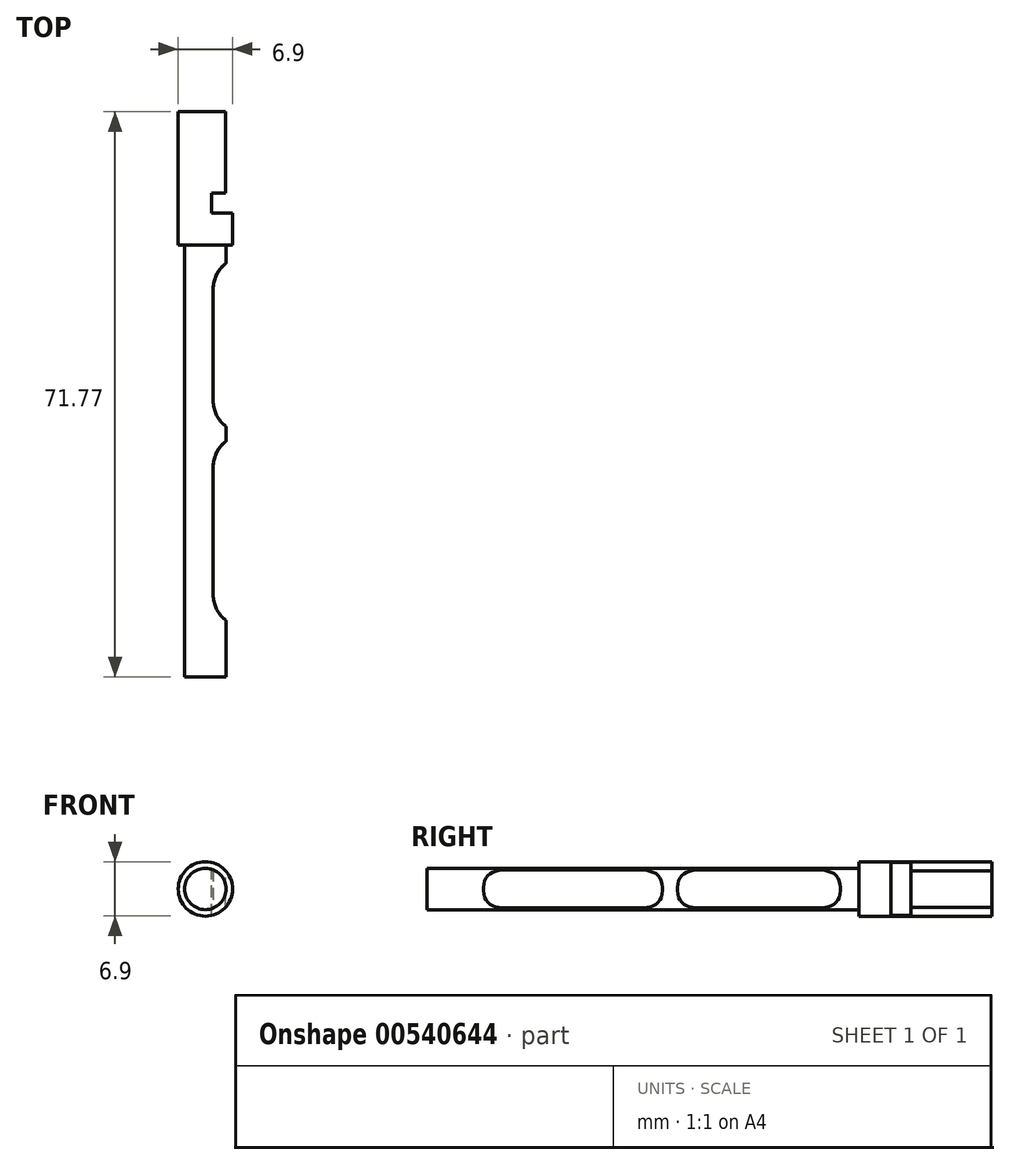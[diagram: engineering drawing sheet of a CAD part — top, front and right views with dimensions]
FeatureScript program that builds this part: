
annotation { "Feature Type Name" : "Feature", "Feature Type Description" : "" }
export const myFeature = defineFeature(function(context is Context, id is Id, definition is map)
    precondition{}
    {
        {
            var Q0;
            Q0=qCreatedBy(makeId("Front.planeOp"),FACE);
            var sketch = newSketch(context, id + "F0", { "sketchPlane" : qUnion([Q0])});
            skCircle(sketch, "E0", {"center": v(0, 0) * mm, "radius": 3.45 * mm});
            skSolve(sketch);
        }
        {
            var Q0;
            Q0 = qSketchRegion(id + "F0", true);
            extrude(context, id + "F1", {"entities" : qUnion([Q0]), "depth" : 71.77 * mm, "offsetDistance" : 25.4 * mm});
        }
        {
            var Q0;
            Q0=qCreatedBy(makeId("Top.planeOp"),FACE);
            cPlane(context, id + "F2", {"entities" : qUnion([Q0]), "cplaneType" : CPlaneType.OFFSET, "offset" : 25.4 * mm, "width" : 152.4 * mm, "height" : 152.4 * mm});
        }
        {
            var Q0;
            Q0=qCreatedBy(id+"F2.planeOp",FACE);
            var sketch = newSketch(context, id + "F3", { "sketchPlane" : qUnion([Q0])});
            skLineSegment(sketch, "E1", {"start": v(0.76, -12.84) * mm, "end": v(5.6, -12.84) * mm});
            skLineSegment(sketch, "E2", {"start": v(0.76, -10.33) * mm, "end": v(5.6, -10.33) * mm});
            skLineSegment(sketch, "E3", {"start": v(0.76, -12.84) * mm, "end": v(0.76, -10.33) * mm});
            skLineSegment(sketch, "E4", {"start": v(5.6, -12.84) * mm, "end": v(5.6, -10.33) * mm});
            skPoint(sketch, "E5.orphan", {"position": v(0.76, 0) * mm});
            skSolve(sketch);
        }
        {
            var Q0;
            Q0=makeQuery(id+"F3.imprint","IMPRINT",FACE,{"disambiguationData":[TD([[makeQuery(id+"F3.imprint","IMPRINT",EDGE,{"derivedFrom":sQuery(id+"F3.wireOp",EDGE,"E1")}),1.0]])]});
            extrude(context, id + "F4", {"entities" : qUnion([Q0]), "operationType" : NewBodyOperationType.REMOVE, "oppositeDirection" : true, "depth" : 39.88 * mm, "offsetDistance" : 25.4 * mm});
        }
        {
            var Q0;
            Q0=qCreatedBy(id+"F2.planeOp",FACE);
            var sketch = newSketch(context, id + "F5", { "sketchPlane" : qUnion([Q0])});
            skLineSegment(sketch, "E6", {"start": v(0, 0) * mm, "end": v(0, -14.35) * mm});
            skLineSegment(sketch, "E7", {"start": v(2.57, 0) * mm, "end": v(2.57, -11.2) * mm});
            skLineSegment(sketch, "E8", {"start": v(2.57, -11.2) * mm, "end": v(5.53, -11.2) * mm});
            skLineSegment(sketch, "E9", {"start": v(5.53, 0) * mm, "end": v(5.53, -11.2) * mm});
            skLineSegment(sketch, "E10", {"start": v(2.57, 0) * mm, "end": v(5.53, 0) * mm});
            skSolve(sketch);
        }
        {
            var Q0;
            Q0 = qSketchRegion(id + "F5", true);
            extrude(context, id + "F6", {"entities" : qUnion([Q0]), "operationType" : NewBodyOperationType.REMOVE, "oppositeDirection" : true, "depth" : 56.64 * mm, "offsetDistance" : 25.4 * mm});
        }
        {
            var Q0;
            Q0=makeQuery(id+"F4.boolean.opBoolean","COPY",FACE,{"derivedFrom":makeQuery(id+"F4.opExtrude","SWEPT_FACE",FACE,{"disambiguationData":[OSD([sQuery(id+"F3.wireOp",EDGE,"E1")])]})});
            cPlane(context, id + "F7", {"entities" : qUnion([Q0]), "cplaneType" : CPlaneType.OFFSET, "offset" : 4.06 * mm, "oppositeDirection" : true, "width" : 152.4 * mm, "height" : 152.4 * mm});
        }
        {
            var Q0;
            Q0=qCreatedBy(id+"F7.planeOp",FACE);
            var sketch = newSketch(context, id + "F8", { "sketchPlane" : qUnion([Q0])});
            skCircle(sketch, "E11", {"center": v(0, 0) * mm, "radius": 2.63 * mm});
            skCircle(sketch, "E12", {"center": v(0, 0) * mm, "radius": 3.45 * mm});
            skSolve(sketch);
        }
        {
            var Q0;
            Q0 = qSketchRegion(id + "F8", true);
            extrude(context, id + "F9", {"entities" : qUnion([Q0]), "operationType" : NewBodyOperationType.REMOVE, "oppositeDirection" : true, "depth" : 58.42 * mm, "offsetDistance" : 25.4 * mm});
        }
        {
            var Q0;
            Q0=qCreatedBy(makeId("Top.planeOp"),FACE);
            var sketch = newSketch(context, id + "F10", { "sketchPlane" : qUnion([Q0])});
            skLineSegment(sketch, "E13.0", {"start": v(1, -45.1) * mm, "end": v(1, -61.36) * mm});
            skArc(sketch, "E14", {"start": v(5.05, -18.43) * mm, "mid": v(2.18, -19.62) * mm, "end": v(1, -22.5) * mm});
            skLineSegment(sketch, "E15", {"start": v(1, -22.5) * mm, "end": v(1, -36.72) * mm});
            skArc(sketch, "E16", {"start": v(1, -36.72) * mm, "mid": v(2.18, -39.6) * mm, "end": v(5.05, -40.78) * mm});
            skArc(sketch, "E17", {"start": v(5.05, -41.04) * mm, "mid": v(2.18, -42.23) * mm, "end": v(1, -45.1) * mm});
            skArc(sketch, "E18", {"start": v(1, -61.36) * mm, "mid": v(2.18, -64.23) * mm, "end": v(5.05, -65.42) * mm});
            skLineSegment(sketch, "E19", {"start": v(5.05, -18.43) * mm, "end": v(5.05, -40.78) * mm});
            skLineSegment(sketch, "E20", {"start": v(5.05, -41.04) * mm, "end": v(5.05, -65.42) * mm});
            skSolve(sketch);
        }
        {
            var Q0;
            Q0 = qSketchRegion(id + "F10", true);
            extrude(context, id + "F11", {"entities" : qUnion([Q0]), "operationType" : NewBodyOperationType.REMOVE, "depth" : 25.4 * mm, "offsetDistance" : 25.4 * mm});
        }
        {
            var Q0;
            Q0=makeQuery(id+"F11.boolean.opBoolean","COPY",FACE,{"derivedFrom":makeQuery(id+"F11.opExtrude","CAP_FACE",FACE,{"disambiguationData":[OSD([sQuery(id+"F10.wireOp",EDGE,"E17"),sQuery(id+"F10.wireOp",EDGE,"E18"),sQuery(id+"F10.wireOp",EDGE,"E20"),sQuery(id+"F10.wireOp",EDGE,"E13.0")])],"isStart":true})});
            var sketch = newSketch(context, id + "F12", { "sketchPlane" : qUnion([Q0])});
            skSolve(sketch);
        }
        {
            var Q0;
            Q0 = qSketchRegion(id + "F12", true);
            var Q1;
            {var subQ0=sQuery(id+"F10.wireOp",EDGE,"E17");Q1=makeQuery(id+"F12.imprint","IMPRINT",FACE,{"disambiguationData":[TD([[makeQuery(id+"F12.imprint","IMPRINT",EDGE,{"derivedFrom":makeQuery(id+"F11.boolean.opBoolean","COPY",EDGE,{"derivedFrom":makeQuery(id+"F11.opExtrude","CAP_EDGE",EDGE,{"disambiguationData":[OSD([subQ0])],"isStart":true})})}),1.0]])]});}
            extrude(context, id + "F13", {"entities" : qUnion([Q0, Q1]), "operationType" : NewBodyOperationType.REMOVE, "oppositeDirection" : true, "depth" : 25.4 * mm, "offsetDistance" : 25.4 * mm});
        }
        {
            var Q0;
            Q0=makeQuery(id+"F11.boolean.opBoolean","COPY",FACE,{"derivedFrom":makeQuery(id+"F11.opExtrude","CAP_FACE",FACE,{"disambiguationData":[OSD([sQuery(id+"F10.wireOp",EDGE,"E14"),sQuery(id+"F10.wireOp",EDGE,"E16"),sQuery(id+"F10.wireOp",EDGE,"E15"),sQuery(id+"F10.wireOp",EDGE,"E19")])],"isStart":true})});
            var sketch = newSketch(context, id + "F14", { "sketchPlane" : qUnion([Q0])});
            skSolve(sketch);
        }
        {
            var Q0;
            Q0 = qSketchRegion(id + "F14", true);
            var Q1;
            {var subQ0=sQuery(id+"F10.wireOp",EDGE,"E14");Q1=makeQuery(id+"F14.imprint","IMPRINT",FACE,{"disambiguationData":[TD([[makeQuery(id+"F14.imprint","IMPRINT",EDGE,{"derivedFrom":makeQuery(id+"F11.boolean.opBoolean","COPY",EDGE,{"derivedFrom":makeQuery(id+"F11.opExtrude","CAP_EDGE",EDGE,{"disambiguationData":[OSD([subQ0])],"isStart":true})})}),1.0]])]});}
            extrude(context, id + "F15", {"entities" : qUnion([Q0, Q1]), "operationType" : NewBodyOperationType.REMOVE, "oppositeDirection" : true, "depth" : 25.4 * mm, "offsetDistance" : 25.4 * mm});
        }
    });
